# Revit family: Indoor_Wall Lamp_Santa&Cole_Cirio
name_source: partatom
category: Luminarias
revit_build: Autodesk Revit 2018 (Build: 20190510_1515(x64)
units: mm (PartAtom-declared; Revit-internal decimal feet)

## family parameters
Compartido = No
Corte con vacíos al cargar = No
Cota de conector redondo = Diámetro de uso
Número OmniClass = 23.80.70.00
Origen de luz = Sí
Punto de cálculo de habitación = No
Se basa en plano de trabajo = Sí
Siempre vertical = No
Tipo de pieza = Normal
Título OmniClass = Lighting

## types (2) — shared parameters
Archivo de red fotométrica = CIRWA02.IES
Assembly instructions - CE = https://www.santacole.com
Assembly instructions - UL = https://www.santacole.com
Cambio de temperatura de color de luz atenuada = <Ninguno>
Carga aparente = 5 VA
Code = CRWA01 / CRWA01D / CRWA02 / CRWA02D / CRWA03 / CRWA03D /
Elevación por defecto = 1219 mm
Energy Label = https://www.santacole.com
Fabricante = Santa & Cole
Filtro de color = 16777215
Manufacturer website = https://www.santacole.com
Technical Information = https://www.santacole.com
URL = https://www.santacole.com
Voltaje (90-305 V) = 220 V
Ángulo de inclinación = 90.00°

## per-type parameters (varying)
| type | CE | Modelo | UL |
| Cirio - CE | Sí | Cirio CE | No |
| Cirio - UL | No | Cirio UL | Sí |

## geometry (parser evidence)
native form markers: Sweep x2
no freeform markers — native parametric forms only
